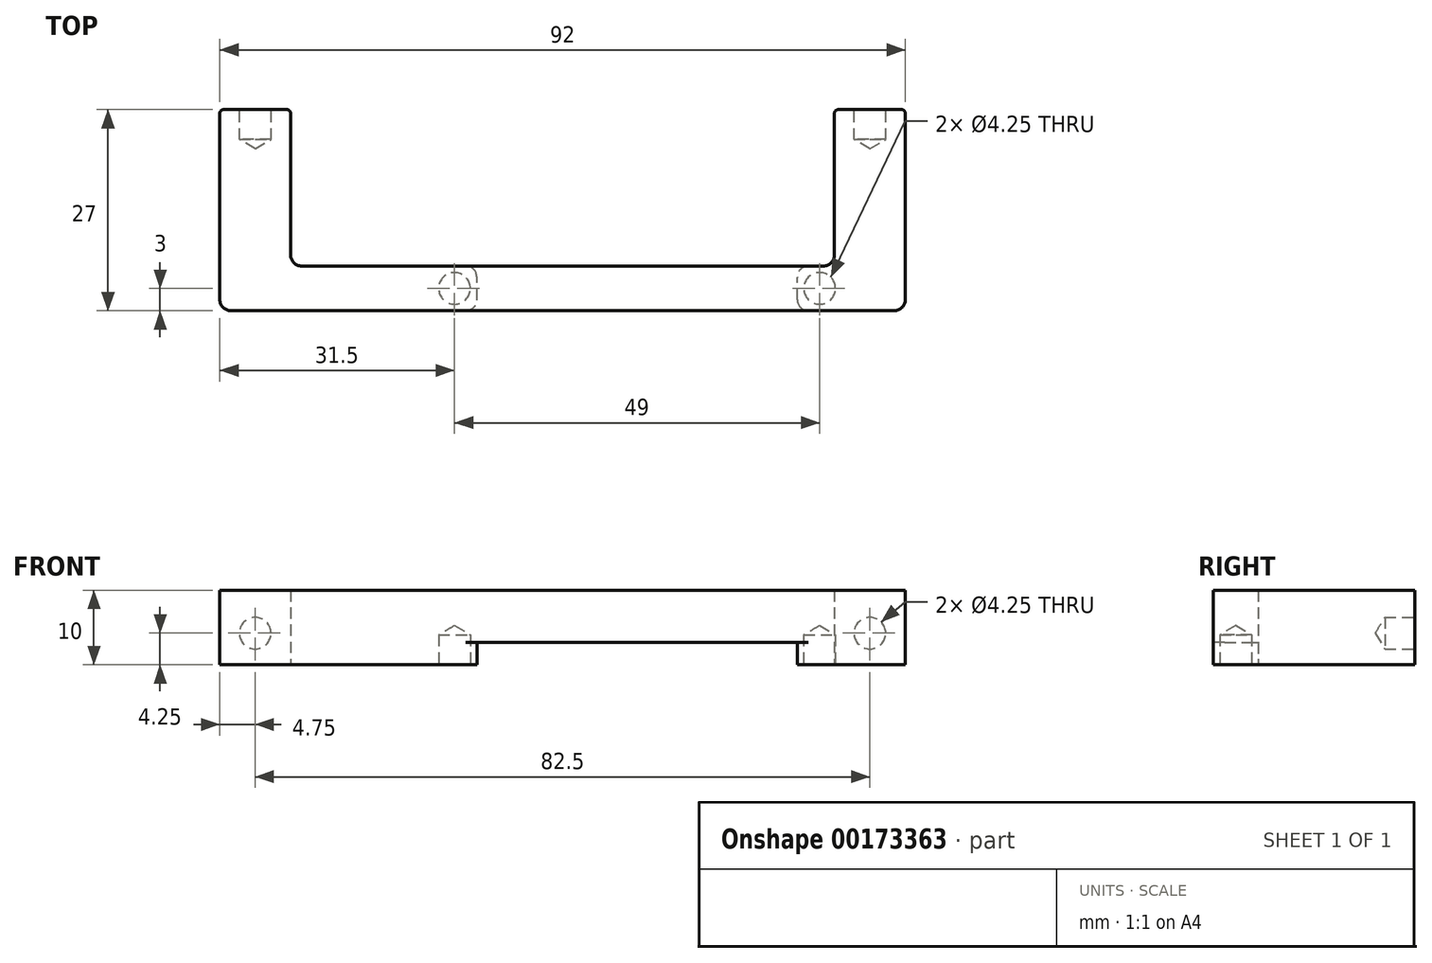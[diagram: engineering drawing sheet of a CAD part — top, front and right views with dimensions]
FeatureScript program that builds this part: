
annotation { "Feature Type Name" : "Feature", "Feature Type Description" : "" }
export const myFeature = defineFeature(function(context is Context, id is Id, definition is map)
    precondition{}
    {
        {
            var Q0;
            Q0=qCreatedBy(makeId("Top.planeOp"),FACE);
            var sketch = newSketch(context, id + "F0", { "sketchPlane" : qUnion([Q0])});
            skLineSegment(sketch, "E0.bottom", {"start": v(-28, 42.5) * mm, "end": v(28, 42.5) * mm});
            skLineSegment(sketch, "E0.top", {"start": v(-28, -42.5) * mm, "end": v(28, -42.5) * mm});
            skLineSegment(sketch, "E0.left", {"start": v(-28, 42.5) * mm, "end": v(-28, -42.5) * mm});
            skLineSegment(sketch, "E0.right", {"start": v(28, 42.5) * mm, "end": v(28, -42.5) * mm});
            skPoint(sketch, "E1", {"position": v(0, 42.5) * mm});
            skPoint(sketch, "E2", {"position": v(-28, 0) * mm});
            skLineSegment(sketch, "E3.bottom", {"start": v(9.75, 45) * mm, "end": v(25.75, 45) * mm});
            skLineSegment(sketch, "E3.top", {"start": v(9.75, 23.75) * mm, "end": v(25.75, 23.75) * mm});
            skLineSegment(sketch, "E3.left", {"start": v(9.75, 45) * mm, "end": v(9.75, 23.75) * mm});
            skLineSegment(sketch, "E3.right", {"start": v(25.75, 45) * mm, "end": v(25.75, 23.75) * mm});
            skPoint(sketch, "E4", {"position": v(17.75, 45) * mm});
            skLineSegment(sketch, "E5.bottom", {"start": v(-8.7, 45) * mm, "end": v(6.7, 45) * mm});
            skLineSegment(sketch, "E5.top", {"start": v(-8.7, 27.5) * mm, "end": v(6.7, 27.5) * mm});
            skLineSegment(sketch, "E5.left", {"start": v(-8.7, 45) * mm, "end": v(-8.7, 27.5) * mm});
            skLineSegment(sketch, "E5.right", {"start": v(6.7, 45) * mm, "end": v(6.7, 27.5) * mm});
            skPoint(sketch, "E6", {"position": v(-1, 45) * mm});
            skLineSegment(sketch, "E7.bottom", {"start": v(-26.7, 45) * mm, "end": v(-11.3, 45) * mm});
            skLineSegment(sketch, "E7.top", {"start": v(-26.7, 27.5) * mm, "end": v(-11.3, 27.5) * mm});
            skLineSegment(sketch, "E7.left", {"start": v(-26.7, 45) * mm, "end": v(-26.7, 27.5) * mm});
            skLineSegment(sketch, "E7.right", {"start": v(-11.3, 45) * mm, "end": v(-11.3, 27.5) * mm});
            skPoint(sketch, "E8", {"position": v(-19, 45) * mm});
            skCircle(sketch, "E9", {"center": v(-24.5, 19) * mm, "radius": 3 * mm});
            skCircle(sketch, "E10", {"center": v(-24.5, -39) * mm, "radius": 3 * mm});
            skCircle(sketch, "E11", {"center": v(24.5, 19) * mm, "radius": 3 * mm});
            skCircle(sketch, "E12", {"center": v(24.5, -39) * mm, "radius": 3 * mm});
            skSolve(sketch);
        }
        {
            var Q0;
            Q0=qCreatedBy(makeId("Top.planeOp"),FACE);
            var sketch = newSketch(context, id + "F1", { "sketchPlane" : qUnion([Q0])});
            skLineSegment(sketch, "E13.bottom", {"start": v(26.5, 43) * mm, "end": v(36, 43) * mm});
            skLineSegment(sketch, "E13.top", {"start": v(26.5, 16) * mm, "end": v(36, 16) * mm});
            skLineSegment(sketch, "E13.left", {"start": v(26.5, 43) * mm, "end": v(26.5, 16) * mm});
            skLineSegment(sketch, "E13.right", {"start": v(36, 43) * mm, "end": v(36, 16) * mm});
            skLineSegment(sketch, "E14.bottom", {"start": v(-46.5, 43) * mm, "end": v(-56, 43) * mm});
            skLineSegment(sketch, "E14.top", {"start": v(-46.5, 16) * mm, "end": v(-56, 16) * mm});
            skLineSegment(sketch, "E14.left", {"start": v(-46.5, 43) * mm, "end": v(-46.5, 16) * mm});
            skLineSegment(sketch, "E14.right", {"start": v(-56, 43) * mm, "end": v(-56, 16) * mm});
            skLineSegment(sketch, "E15.bottom", {"start": v(-46.5, 16) * mm, "end": v(-21.5, 16) * mm});
            skLineSegment(sketch, "E15.top", {"start": v(-46.5, 22) * mm, "end": v(-21.5, 22) * mm});
            skLineSegment(sketch, "E15.left", {"start": v(-46.5, 16) * mm, "end": v(-46.5, 22) * mm});
            skLineSegment(sketch, "E15.right", {"start": v(-21.5, 16) * mm, "end": v(-21.5, 22) * mm});
            skLineSegment(sketch, "E16.bottom", {"start": v(26.5, 16) * mm, "end": v(21.5, 16) * mm});
            skLineSegment(sketch, "E16.top", {"start": v(26.5, 22) * mm, "end": v(21.5, 22) * mm});
            skLineSegment(sketch, "E16.left", {"start": v(26.5, 16) * mm, "end": v(26.5, 22) * mm});
            skLineSegment(sketch, "E16.right", {"start": v(21.5, 16) * mm, "end": v(21.5, 22) * mm});
            skLineSegment(sketch, "E17.bottom", {"start": v(21.5, 22) * mm, "end": v(-21.5, 22) * mm});
            skLineSegment(sketch, "E17.top", {"start": v(21.5, 16) * mm, "end": v(-21.5, 16) * mm});
            skLineSegment(sketch, "E17.left", {"start": v(21.5, 22) * mm, "end": v(21.5, 16) * mm});
            skLineSegment(sketch, "E17.right", {"start": v(-21.5, 22) * mm, "end": v(-21.5, 16) * mm});
            skPoint(sketch, "E18", {"position": v(-51.25, 43) * mm});
            skPoint(sketch, "E19", {"position": v(31.25, 43) * mm});
            skSolve(sketch);
        }
        {
            var Q0;
            Q0=makeQuery(id+"F1.imprint","IMPRINT",FACE,{"disambiguationData":[TD([[makeQuery(id+"F1.imprint","IMPRINT",EDGE,{"derivedFrom":sQuery(id+"F1.wireOp",EDGE,"E13.bottom")}),-1.0]])]});
            var Q1;
            Q1=makeQuery(id+"F1.imprint","IMPRINT",FACE,{"disambiguationData":[TD([[makeQuery(id+"F1.imprint","IMPRINT",EDGE,{"derivedFrom":sQuery(id+"F1.wireOp",EDGE,"E14.bottom")}),1.0]])]});
            var Q2;
            Q2=makeQuery(id+"F1.imprint","IMPRINT",FACE,{"disambiguationData":[TD([[makeQuery(id+"F1.imprint","IMPRINT",EDGE,{"derivedFrom":sQuery(id+"F1.wireOp",EDGE,"E15.bottom")}),1.0]])]});
            var Q3;
            Q3=makeQuery(id+"F1.imprint","IMPRINT",FACE,{"disambiguationData":[TD([[makeQuery(id+"F1.imprint","IMPRINT",EDGE,{"derivedFrom":sQuery(id+"F1.wireOp",EDGE,"E16.bottom")}),-1.0]])]});
            extrude(context, id + "F2", {"entities" : qUnion([Q0, Q1, Q2, Q3]), "depth" : 10 * mm});
        }
        {
            var Q0;
            Q0=makeQuery(id+"F1.imprint","IMPRINT",FACE,{"disambiguationData":[TD([[makeQuery(id+"F1.imprint","IMPRINT",EDGE,{"derivedFrom":sQuery(id+"F1.wireOp",EDGE,"E17.bottom")}),1.0]])]});
            extrude(context, id + "F3", {"entities" : qUnion([Q0]), "operationType" : NewBodyOperationType.ADD, "depth" : 10 * mm, "hasSecondDirection" : true, "secondDirectionOppositeDirection" : false, "secondDirectionDepth" : 3 * mm});
        }
        {
            var Q0;
            Q0=makeQuery(id+"F2.opExtrude","SWEPT_FACE",FACE,{"disambiguationData":[OSD([sQuery(id+"F1.wireOp",EDGE,"E14.bottom")])]});
            var sketch = newSketch(context, id + "F4", { "sketchPlane" : qUnion([Q0])});
            skCircle(sketch, "E20", {"center": v(-31.25, 4.25) * mm, "radius": 2.12 * mm});
            skPoint(sketch, "E20.centerSnap0", {"position": v(-31.25, 0) * mm});
            skCircle(sketch, "E21", {"center": v(51.25, 4.25) * mm, "radius": 2.12 * mm});
            skPoint(sketch, "E21.centerSnap0", {"position": v(51.25, 0) * mm});
            skSolve(sketch);
        }
        {
            var Q0;
            Q0=sQuery(id+"F4.wireOp",VERTEX,"E20.center");
            var Q1;
            Q1=sQuery(id+"F4.wireOp",VERTEX,"E21.center");
            var Q2;
            Q2=makeQuery(id+"F2.opExtrude","SWEPT_BODY",BODY,{"disambiguationData":[OSD([sQuery(id+"F1.wireOp",EDGE,"E13.bottom"),sQuery(id+"F1.wireOp",EDGE,"E13.top"),sQuery(id+"F1.wireOp",EDGE,"E13.left"),sQuery(id+"F1.wireOp",EDGE,"E13.right"),sQuery(id+"F1.wireOp",EDGE,"E16.bottom"),sQuery(id+"F1.wireOp",EDGE,"E16.top"),sQuery(id+"F1.wireOp",EDGE,"E17.left")])]});
            hole(context, id + "F5", {"style" : HoleStyle.SIMPLE, "endStyle" : HoleEndStyle.BLIND, "holeDiameter" : 4.25 * mm, "holeDepth" : 4 * mm, "locations" : qUnion([Q0, Q1]), "scope" : qUnion([Q2])});
        }
        {
            var Q0;
            Q0=sQuery(id+"F0.wireOp",VERTEX,"E11.center");
            var Q1;
            Q1=sQuery(id+"F0.wireOp",VERTEX,"E9.center");
            var Q2;
            Q2=makeQuery(id+"F2.opExtrude","SWEPT_BODY",BODY,{"disambiguationData":[OSD([sQuery(id+"F1.wireOp",EDGE,"E13.bottom"),sQuery(id+"F1.wireOp",EDGE,"E13.top"),sQuery(id+"F1.wireOp",EDGE,"E13.left"),sQuery(id+"F1.wireOp",EDGE,"E13.right"),sQuery(id+"F1.wireOp",EDGE,"E16.bottom"),sQuery(id+"F1.wireOp",EDGE,"E16.top"),sQuery(id+"F1.wireOp",EDGE,"E17.left")])]});
            hole(context, id + "F6", {"style" : HoleStyle.SIMPLE, "endStyle" : HoleEndStyle.BLIND, "oppositeDirection" : true, "holeDiameter" : 4.25 * mm, "holeDepth" : 4 * mm, "locations" : qUnion([Q0, Q1]), "scope" : qUnion([Q2])});
        }
        {
            var Q0;
            Q0=makeQuery(id+"F2.opExtrude","SWEPT_EDGE",EDGE,{"disambiguationData":[OSD([sQuery(id+"F1.wireOp",EDGE,"E13.left"),sQuery(id+"F1.wireOp",EDGE,"E16.top"),sQuery(id+"F1.wireOp",EDGE,"E16.left")])]});
            var Q1;
            Q1=makeQuery(id+"F2.opExtrude","SWEPT_EDGE",EDGE,{"disambiguationData":[OSD([sQuery(id+"F1.wireOp",EDGE,"E14.left"),sQuery(id+"F1.wireOp",EDGE,"E15.top"),sQuery(id+"F1.wireOp",EDGE,"E15.left")])]});
            var Q2;
            Q2=makeQuery(id+"F2.opExtrude","SWEPT_EDGE",EDGE,{"disambiguationData":[OSD([sQuery(id+"F1.wireOp",EDGE,"E13.top"),sQuery(id+"F1.wireOp",EDGE,"E13.right")])]});
            var Q3;
            Q3=makeQuery(id+"F2.opExtrude","SWEPT_EDGE",EDGE,{"disambiguationData":[OSD([sQuery(id+"F1.wireOp",EDGE,"E14.top"),sQuery(id+"F1.wireOp",EDGE,"E14.right")])]});
            var Q4;
            Q4=makeQuery(id+"F2.opExtrude","SWEPT_EDGE",EDGE,{"disambiguationData":[OSD([sQuery(id+"F1.wireOp",EDGE,"E16.top"),sQuery(id+"F1.wireOp",EDGE,"E17.bottom"),sQuery(id+"F1.wireOp",EDGE,"E17.left")])]});
            var Q5;
            Q5=makeQuery(id+"F2.opExtrude","SWEPT_EDGE",EDGE,{"disambiguationData":[OSD([sQuery(id+"F1.wireOp",EDGE,"E16.bottom"),sQuery(id+"F1.wireOp",EDGE,"E17.top"),sQuery(id+"F1.wireOp",EDGE,"E17.left")])]});
            var Q6;
            Q6=makeQuery(id+"F2.opExtrude","SWEPT_EDGE",EDGE,{"disambiguationData":[OSD([sQuery(id+"F1.wireOp",EDGE,"E15.top"),sQuery(id+"F1.wireOp",EDGE,"E17.bottom"),sQuery(id+"F1.wireOp",EDGE,"E17.right")])]});
            var Q7;
            Q7=makeQuery(id+"F2.opExtrude","SWEPT_EDGE",EDGE,{"disambiguationData":[OSD([sQuery(id+"F1.wireOp",EDGE,"E15.bottom"),sQuery(id+"F1.wireOp",EDGE,"E17.top"),sQuery(id+"F1.wireOp",EDGE,"E17.right")])]});
            fillet(context, id + "F7", {"entities" : qUnion([Q0, Q1, Q2, Q3, Q4, Q5, Q6, Q7]), "radius" : 1.5 * mm, "tangentPropagation" : true, "allowEdgeOverflow" : false});
        }
        {
            var Q0;
            Q0=makeQuery(id+"F2.opExtrude","SWEPT_EDGE",EDGE,{"disambiguationData":[OSD([sQuery(id+"F1.wireOp",EDGE,"E13.bottom"),sQuery(id+"F1.wireOp",EDGE,"E13.right")])]});
            var Q1;
            Q1=makeQuery(id+"F2.opExtrude","SWEPT_EDGE",EDGE,{"disambiguationData":[OSD([sQuery(id+"F1.wireOp",EDGE,"E13.bottom"),sQuery(id+"F1.wireOp",EDGE,"E13.left")])]});
            var Q2;
            Q2=makeQuery(id+"F2.opExtrude","SWEPT_EDGE",EDGE,{"disambiguationData":[OSD([sQuery(id+"F1.wireOp",EDGE,"E14.bottom"),sQuery(id+"F1.wireOp",EDGE,"E14.left")])]});
            var Q3;
            Q3=makeQuery(id+"F2.opExtrude","SWEPT_EDGE",EDGE,{"disambiguationData":[OSD([sQuery(id+"F1.wireOp",EDGE,"E14.bottom"),sQuery(id+"F1.wireOp",EDGE,"E14.right")])]});
            fillet(context, id + "F8", {"entities" : qUnion([Q0, Q1, Q2, Q3]), "radius" : .5 * mm, "tangentPropagation" : true, "allowEdgeOverflow" : false});
        }
    });
